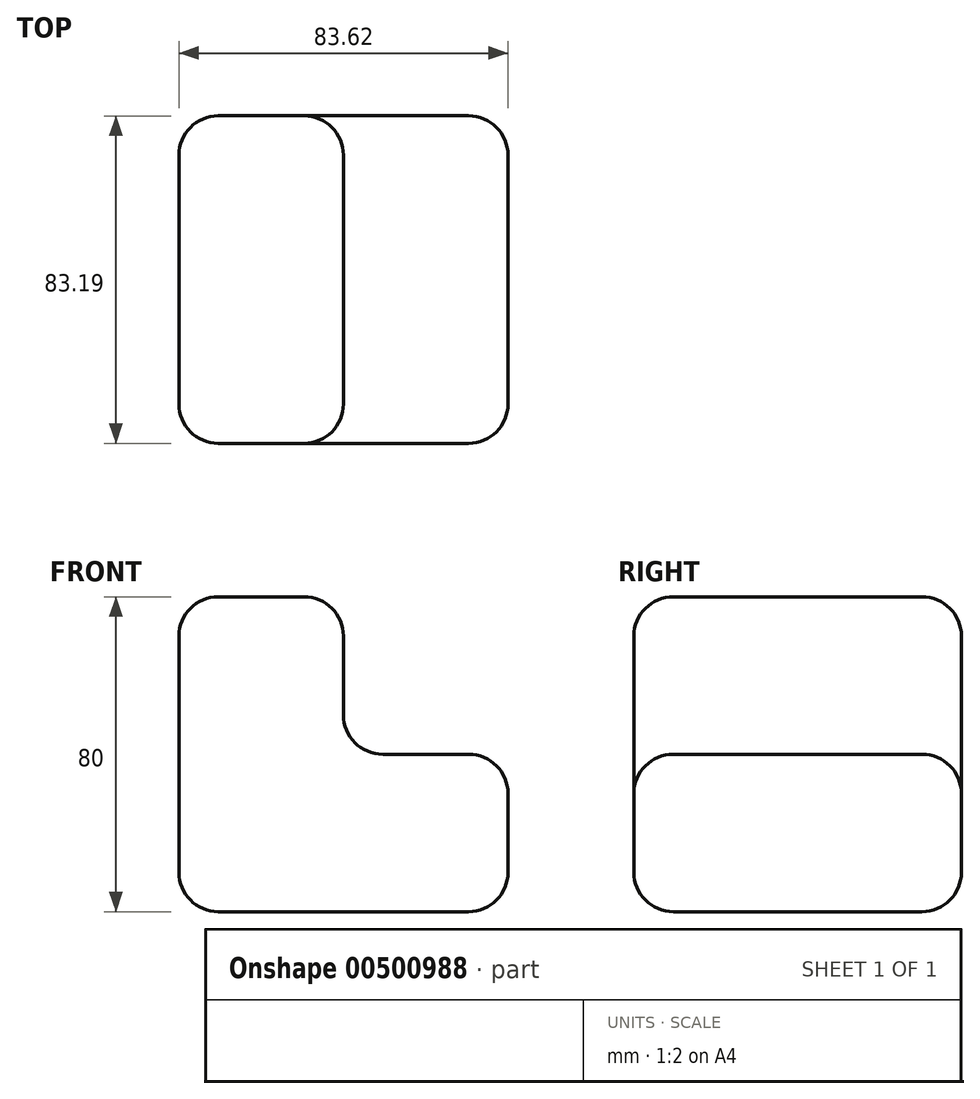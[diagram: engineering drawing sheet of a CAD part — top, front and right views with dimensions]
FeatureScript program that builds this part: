
annotation { "Feature Type Name" : "Feature", "Feature Type Description" : "" }
export const myFeature = defineFeature(function(context is Context, id is Id, definition is map)
    precondition{}
    {
        {
            var Q0;
            Q0=qCreatedBy(makeId("Top.planeOp"),FACE);
            var sketch = newSketch(context, id + "F0", { "sketchPlane" : qUnion([Q0])});
            skLineSegment(sketch, "E0.bottom", {"start": v(-59.13, -45.93) * mm, "end": v(24.5, -45.93) * mm});
            skLineSegment(sketch, "E0.top", {"start": v(-59.13, 37.26) * mm, "end": v(24.5, 37.26) * mm});
            skLineSegment(sketch, "E0.left", {"start": v(-59.13, -45.93) * mm, "end": v(-59.13, 37.26) * mm});
            skLineSegment(sketch, "E0.right", {"start": v(24.5, -45.93) * mm, "end": v(24.5, 37.26) * mm});
            skSolve(sketch);
        }
        {
            var Q0;
            Q0=makeQuery(id+"F0.imprint","IMPRINT",FACE,{"disambiguationData":[TD([[makeQuery(id+"F0.imprint","IMPRINT",EDGE,{"derivedFrom":sQuery(id+"F0.wireOp",EDGE,"E0.bottom")}),1.0]])]});
            extrude(context, id + "F1", {"entities" : qUnion([Q0]), "depth" : 40 * mm});
        }
        {
            var Q0;
            Q0=makeQuery(id+"F1.opExtrude","CAP_FACE",FACE,{"disambiguationData":[OSD([sQuery(id+"F0.wireOp",EDGE,"E0.bottom"),sQuery(id+"F0.wireOp",EDGE,"E0.top"),sQuery(id+"F0.wireOp",EDGE,"E0.left"),sQuery(id+"F0.wireOp",EDGE,"E0.right")])],"isStart":false});
            var sketch = newSketch(context, id + "F2", { "sketchPlane" : qUnion([Q0])});
            skLineSegment(sketch, "E1", {"start": v(-17.32, 37.26) * mm, "end": v(-17.32, -45.93) * mm});
            skSolve(sketch);
        }
        {
            var Q0;
            {var subQ1=sQuery(id+"F2.wireOp",EDGE,"E1");Q0=makeQuery(id+"F2.imprint","IMPRINT",FACE,{"disambiguationData":[TD([[makeQuery(id+"F2.imprint","IMPRINT",EDGE,{"derivedFrom":subQ1}),-1.0]])]});}
            extrude(context, id + "F3", {"entities" : qUnion([Q0]), "operationType" : NewBodyOperationType.ADD, "depth" : 40 * mm});
        }
        {
            var Q0;
            Q0=makeQuery(id+"F3.opExtrude","CAP_FACE",FACE,{"disambiguationData":[OSD([sQuery(id+"F0.wireOp",EDGE,"E0.bottom"),sQuery(id+"F0.wireOp",EDGE,"E0.top"),sQuery(id+"F0.wireOp",EDGE,"E0.left"),sQuery(id+"F2.wireOp",EDGE,"E1")])],"isStart":false});
            var Q1;
            {var subQ0=sQuery(id+"F0.wireOp",EDGE,"E0.bottom");Q1=makeQuery(id+"F3.boolean.opBoolean","MERGE",FACE,{"derivedFrom":[makeQuery(id+"F1.opExtrude","SWEPT_FACE",FACE,{"disambiguationData":[OSD([subQ0])]}),makeQuery(id+"F3.opExtrude","SWEPT_FACE",FACE,{"disambiguationData":[OSD([subQ0])]})]});}
            var Q2;
            Q2=makeQuery(id+"F3.opExtrude","SWEPT_FACE",FACE,{"disambiguationData":[OSD([sQuery(id+"F2.wireOp",EDGE,"E1")])]});
            var Q3;
            Q3=makeQuery(id+"F1.opExtrude","CAP_FACE",FACE,{"disambiguationData":[OSD([sQuery(id+"F0.wireOp",EDGE,"E0.bottom"),sQuery(id+"F0.wireOp",EDGE,"E0.top"),sQuery(id+"F0.wireOp",EDGE,"E0.left"),sQuery(id+"F0.wireOp",EDGE,"E0.right")])],"isStart":false});
            var Q4;
            Q4=makeQuery(id+"F1.opExtrude","SWEPT_FACE",FACE,{"disambiguationData":[OSD([sQuery(id+"F0.wireOp",EDGE,"E0.right")])]});
            var Q5;
            {var subQ0=sQuery(id+"F0.wireOp",EDGE,"E0.top");Q5=makeQuery(id+"F3.boolean.opBoolean","MERGE",FACE,{"derivedFrom":[makeQuery(id+"F1.opExtrude","SWEPT_FACE",FACE,{"disambiguationData":[OSD([subQ0])]}),makeQuery(id+"F3.opExtrude","SWEPT_FACE",FACE,{"disambiguationData":[OSD([subQ0])]})]});}
            var Q6;
            Q6=makeQuery(id+"F1.opExtrude","CAP_FACE",FACE,{"disambiguationData":[OSD([sQuery(id+"F0.wireOp",EDGE,"E0.bottom"),sQuery(id+"F0.wireOp",EDGE,"E0.top"),sQuery(id+"F0.wireOp",EDGE,"E0.left"),sQuery(id+"F0.wireOp",EDGE,"E0.right")])],"isStart":true});
            var Q7;
            {var subQ0=sQuery(id+"F0.wireOp",EDGE,"E0.left");Q7=makeQuery(id+"F3.boolean.opBoolean","MERGE",FACE,{"derivedFrom":[makeQuery(id+"F1.opExtrude","SWEPT_FACE",FACE,{"disambiguationData":[OSD([subQ0])]}),makeQuery(id+"F3.opExtrude","SWEPT_FACE",FACE,{"disambiguationData":[OSD([subQ0])]})]});}
            fillet(context, id + "F4", {"entities" : qUnion([Q0, Q1, Q2, Q3, Q4, Q5, Q6, Q7]), "radius" : 10 * mm, "tangentPropagation" : true, "allowEdgeOverflow" : false});
        }
    });
